# Revit family: Shower_Trim-DXV-Oak_Hill-D35155537_Series
name_source: partatom
category: Plumbing Fixtures
units: mm (PartAtom-declared; Revit-internal decimal feet)

## family parameters
Cut with Voids When Loaded = No
Host = Face
OmniClass Number = 23.45.05.14.17
OmniClass Title = Showers
Part Type = Normal
Room Calculation Point = No
Round Connector Dimension = Use Diameter
Shared = Yes

## types (4) — shared parameters
ADA Compliant = Yes
Assembly Code = D2010710
CW Connection = Yes
CWFU = 3
Cold Water Connection Diameter = 1/2"
Cold Water Connection Radius = 1/4"
Default Elevation = 48"
Description = 3-Handle Thermostatic Valve Trim
HW Connection = Yes
HWFU = 3
Height = 11 3/4"
Hot Water Connection Diameter = 1/2"
Hot Water Connection Radius = 1/4"
Installation Type = Wall Mount
Length = 2 5/8"
Manufacturer = DXV
Price = Prices may vary. Please consult Manufacturer Representative for most up-to-date price list.
Shower Rough Valve = See spec sheet for required valve options
Tempered Water Connection = Yes
Tempered Water Connection Diameter = 1/2"
Tempered Water Connection Radius = 1/4"
URL = https://www.dxv.com
Vent Connection = No
WFU = 4
Waste Connection = No
Width = 3 3/4"

## per-type parameters (varying)
| type | Finish | Material |
| D35155537.100 | Brass-DXV-100-Polished Chrome | Brass-DXV-100-Polished Chrome |
| D35155537.144 | Brass-DXV-144-Brushed Nickel | Brass-DXV-144-Brushed Nickel |
| D35155537.150 | Brass-DXV-150-Platinum Nickel | Brass-DXV-150-Platinum Nickel |
| D35155537.427 | Brass-DXV-427-Satin Brass | Brass-DXV-427-Satin Brass |

note: column(s) folded — value = type name in every type: Model

## geometry (parser evidence)
native form markers: Sweep x2
no freeform markers — native parametric forms only
